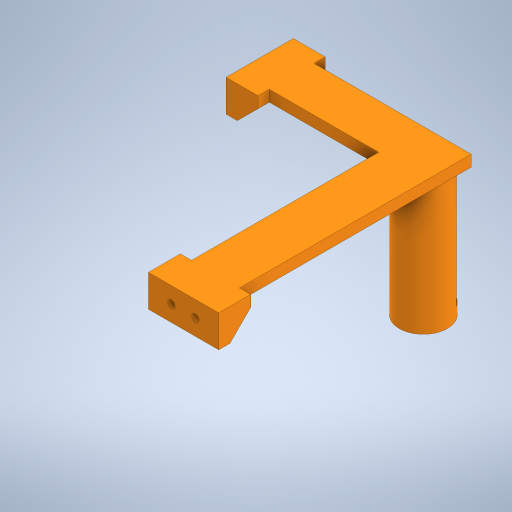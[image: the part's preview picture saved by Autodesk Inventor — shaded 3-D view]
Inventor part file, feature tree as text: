
AUTODESK INVENTOR PART (.ipt)
format: ipt  version: 2023 (Build 270158000, 158)  size: 379,392 bytes
history: native  units: mm
features: extrude x13, sketch x13, other x3, projected_geometry x2, reference x1
ambient origin geometry x8: Origin, YZ Plane, XZ Plane, XY Plane, X Axis, Y Axis, Z Axis, Center Point
bodies: Solid1 (feature_tree)
feature tree (32):
  extrude  "Extrusion1"  Depth=20.0mm
  extrude  "Extrusion2"  Depth=150.0mm
  sketch  "Sketch3"  dims[d4=30.0mm d5=0.0mm d6=80.0mm d7=7.0mm d8=0.0mm d9=0.0mm]
  extrude  "Extrusion3"  Depth=80.0mm TaperAngle=0.0deg
  extrude  "Extrusion4"  Depth=10.0mm
  extrude  "Extrusion5"  Depth=10.0mm
  extrude  "Extrusion6"  Depth=15.0mm
  extrude  "Extrusion7"  Depth=7.0mm TaperAngle=0.0deg
  extrude  "Extrusion8"  Depth=7.0mm TaperAngle=0.0deg
  extrude  "Extrusion9"  Depth=11.0mm
  extrude  "Extrusion10"  Depth=80.0mm
  extrude  "Extrusion11"  Depth=7.0mm TaperAngle=0.0deg
  extrude  "Extrusion12"  Depth=15.0mm
  extrude  "Extrusion13"  Depth=7.0mm TaperAngle=0.0deg
  sketch  "Sketch1"  dims[d0=7.0mm d1=20.0mm]
  sketch  "Sketch2"  dims[d2=7.0mm d3=150.0mm]
  sketch  "Sketch4"  dims[d10=10.0mm d11=4.5mm]
  projected_geometry  "Projected Loop1"
  sketch  "Sketch5"  dims[d12=4.5mm d13=10.0mm]
  projected_geometry  "Projected Loop2"
  sketch  "Sketch6"  dims[d14=15.0mm d15=7.5mm]
  sketch  "Sketch7"  dims[d16=13.0mm d17=7.0mm d18=0.0mm]
  sketch  "Sketch8"  dims[d19=7.0mm d20=0.0mm d21=7.0mm d22=0.0mm]
  reference  "Reference1"
  sketch  "Sketch9"  dims[d23=11.0mm d24=11.0mm]
  sketch  "Sketch10"  dims[d25=12.0mm d26=0.0mm d27=80.0mm]
  sketch  "Sketch11"  dims[d28=7.0mm d29=72.0mm d30=0.0mm]
  sketch  "Sketch13"  dims[d31=0.0mm d32=15.0mm]
  sketch  "Sketch15"  dims[d33=20.0mm d34=7.0mm d35=0.0mm d36=7.0mm d37=0.0mm d38=7.0mm d39=7.0mm d40=13.0mm d41=7.0mm d42=0.0mm d43=0.0mm d44=45.0deg d45=7.0mm d46=0.0mm d47=7.0mm d48=0.0mm d49=10.0mm d50=10.0mm d51=15.0mm d52=6.5mm d53=6.507214mm d54=4.5mm d55=4.5mm d56=7.0mm d57=0.0mm d58=10.0mm d59=10.0mm d60=20.0mm d61=0.0mm]
  other  "<userpath>\OneDrive\ClawdDrive\Objet3D\3DPrinter\inventor\3DPrinterBeltCoreXY.iam"
  other  "3DPrinterBeltCoreXY.iam"
  other  "20X20 - T-slot - Vertical:2"
